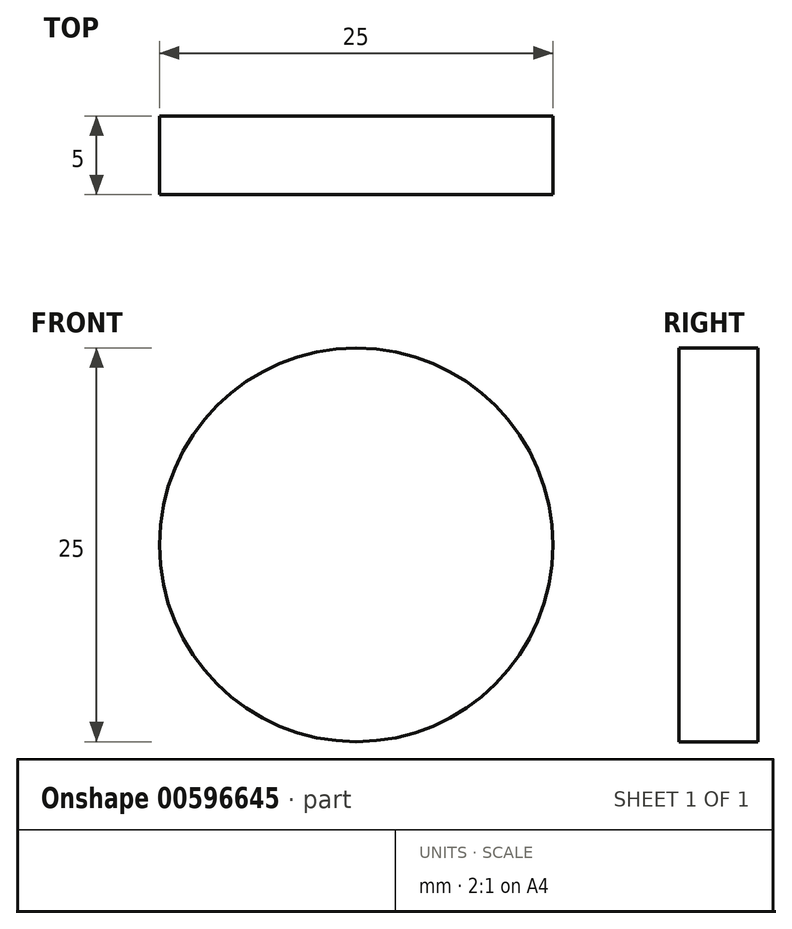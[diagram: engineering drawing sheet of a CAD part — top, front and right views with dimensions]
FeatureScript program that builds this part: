
annotation { "Feature Type Name" : "Feature", "Feature Type Description" : "" }
export const myFeature = defineFeature(function(context is Context, id is Id, definition is map)
    precondition{}
    {
        {
            var Q0;
            Q0=qCreatedBy(makeId("Front.planeOp"),FACE);
            var sketch = newSketch(context, id + "F0", { "sketchPlane" : qUnion([Q0])});
            skCircle(sketch, "E0", {"center": v(0, 0) * mm, "radius": 12.5 * mm});
            skSolve(sketch);
        }
        {
            var Q0;
            Q0=makeQuery(id+"F0.imprint","IMPRINT",FACE,{"disambiguationData":[TD([[makeQuery(id+"F0.imprint","IMPRINT",EDGE,{"derivedFrom":sQuery(id+"F0.wireOp",EDGE,"E0")}),1.0]])]});
            extrude(context, id + "F1", {"entities" : qUnion([Q0]), "depth" : 5 * mm, "offsetDistance" : 25 * mm});
        }
    });
